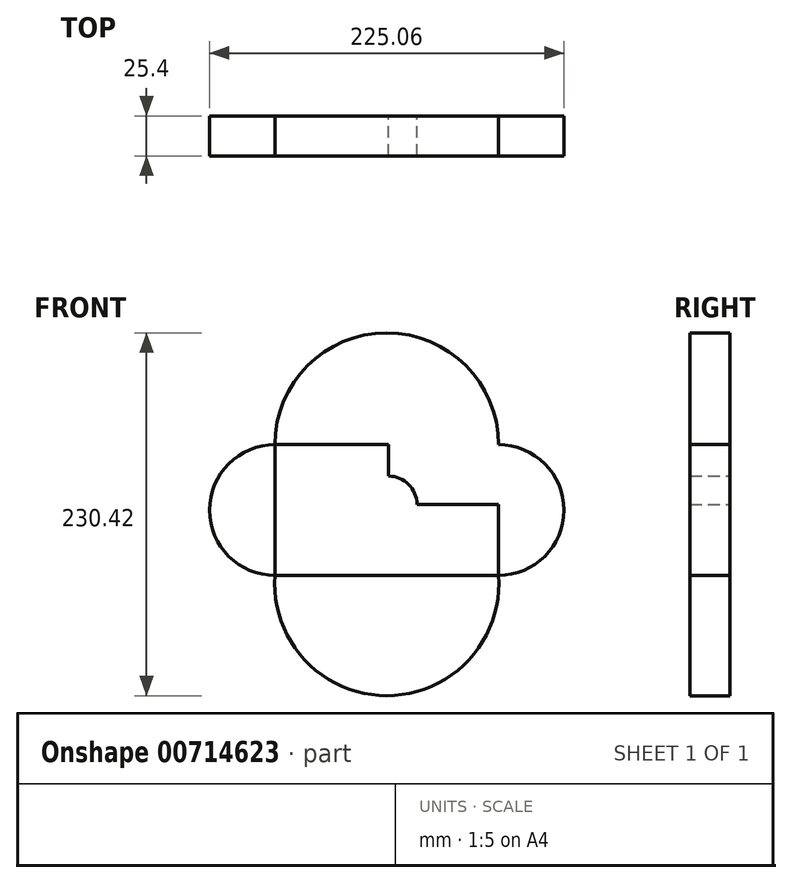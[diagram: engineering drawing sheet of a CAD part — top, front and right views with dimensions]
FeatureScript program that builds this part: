
annotation { "Feature Type Name" : "Feature", "Feature Type Description" : "" }
export const myFeature = defineFeature(function(context is Context, id is Id, definition is map)
    precondition{}
    {
        {
            var Q0;
            Q0=qCreatedBy(makeId("Front.planeOp"),FACE);
            var sketch = newSketch(context, id + "F0", { "sketchPlane" : qUnion([Q0])});
            skLineSegment(sketch, "E0.bottom", {"start": v(-72.25, 37.87) * mm, "end": v(69.73, 37.87) * mm});
            skLineSegment(sketch, "E0.top", {"start": v(-72.25, -45.22) * mm, "end": v(69.73, -45.22) * mm});
            skLineSegment(sketch, "E0.left", {"start": v(-72.25, 37.87) * mm, "end": v(-72.25, -45.22) * mm});
            skLineSegment(sketch, "E0.right", {"start": v(69.73, 37.87) * mm, "end": v(69.73, -45.22) * mm});
            skLineSegment(sketch, "E1.bottom", {"start": v(69.73, 37.87) * mm, "end": v(-51.39, 37.87) * mm});
            skLineSegment(sketch, "E1.top", {"start": v(69.73, -29.61) * mm, "end": v(-51.39, -29.61) * mm});
            skLineSegment(sketch, "E1.left", {"start": v(69.73, 37.87) * mm, "end": v(69.73, -29.61) * mm});
            skLineSegment(sketch, "E1.right", {"start": v(-51.39, 37.87) * mm, "end": v(-51.39, -29.61) * mm});
            skLineSegment(sketch, "E2.bottom", {"start": v(0, 0) * mm, "end": v(69.73, 0) * mm});
            skLineSegment(sketch, "E2.top", {"start": v(0, 37.87) * mm, "end": v(69.73, 37.87) * mm});
            skLineSegment(sketch, "E2.left", {"start": v(0, 0) * mm, "end": v(0, 37.87) * mm});
            skLineSegment(sketch, "E2.right", {"start": v(69.73, 0) * mm, "end": v(69.73, 37.87) * mm});
            skCircle(sketch, "E3", {"center": v(0, 0) * mm, "radius": 17.93 * mm});
            skArc(sketch, "E4", {"start": v(69.73, 37.87) * mm, "mid": v(-1.26, 108.86) * mm, "end": v(-72.25, 37.87) * mm});
            skArc(sketch, "E5", {"start": v(-72.25, -45.22) * mm, "mid": v(-1.26, -121.56) * mm, "end": v(69.73, -45.22) * mm});
            skArc(sketch, "E6", {"start": v(69.73, -45.22) * mm, "mid": v(111.27, -3.67) * mm, "end": v(69.73, 37.87) * mm});
            skArc(sketch, "E7", {"start": v(-72.25, 37.87) * mm, "mid": v(-113.8, -3.67) * mm, "end": v(-72.25, -45.22) * mm});
            skSolve(sketch);
        }
        {
            var Q0;
            Q0=makeQuery(id+"F0.imprint","IMPRINT",FACE,{"disambiguationData":[TD([[makeQuery(id+"F0.imprint","IMPRINT",EDGE,{"derivedFrom":sQuery(id+"F0.wireOp",EDGE,"E0.bottom")}),1.0]])]});
            var Q1;
            Q1=makeQuery(id+"F0.imprint","IMPRINT",FACE,{"disambiguationData":[TD([[makeQuery(id+"F0.imprint","IMPRINT",EDGE,{"derivedFrom":sQuery(id+"F0.wireOp",EDGE,"E0.left")}),-1.0]])]});
            var Q2;
            {var subQ1=sQuery(id+"F0.wireOp",EDGE,"E1.bottom");Q2=makeQuery(id+"F0.imprint","IMPRINT",FACE,{"disambiguationData":[TD([[makeQuery(id+"F0.imprint","IMPRINT",EDGE,{"derivedFrom":subQ1}),1.0]])]});}
            var Q3;
            Q3=makeQuery(id+"F0.imprint","IMPRINT",FACE,{"disambiguationData":[TD([[makeQuery(id+"F0.imprint","IMPRINT",EDGE,{"derivedFrom":sQuery(id+"F0.wireOp",EDGE,"E0.bottom")}),-1.0]])]});
            var Q4;
            Q4=makeQuery(id+"F0.imprint","IMPRINT",FACE,{"disambiguationData":[TD([[makeQuery(id+"F0.imprint","IMPRINT",EDGE,{"derivedFrom":sQuery(id+"F0.wireOp",EDGE,"E0.top")}),-1.0]])]});
            var Q5;
            Q5=makeQuery(id+"F0.imprint","IMPRINT",FACE,{"disambiguationData":[TD([[makeQuery(id+"F0.imprint","IMPRINT",EDGE,{"derivedFrom":sQuery(id+"F0.wireOp",EDGE,"E0.right")}),1.0]])]});
            var Q6;
            {var subQ2=sQuery(id+"F0.wireOp",EDGE,"E2.top");Q6=makeQuery(id+"F0.imprint","IMPRINT",FACE,{"disambiguationData":[TD([[makeQuery(id+"F0.imprint","IMPRINT",EDGE,{"derivedFrom":subQ2}),-1.0]])]});}
            extrude(context, id + "F1", {"entities" : qUnion([Q0, Q1, Q2, Q3, Q4, Q5, Q6]), "depth" : 25.4 * mm, "offsetDistance" : 25.4 * mm});
        }
    });
